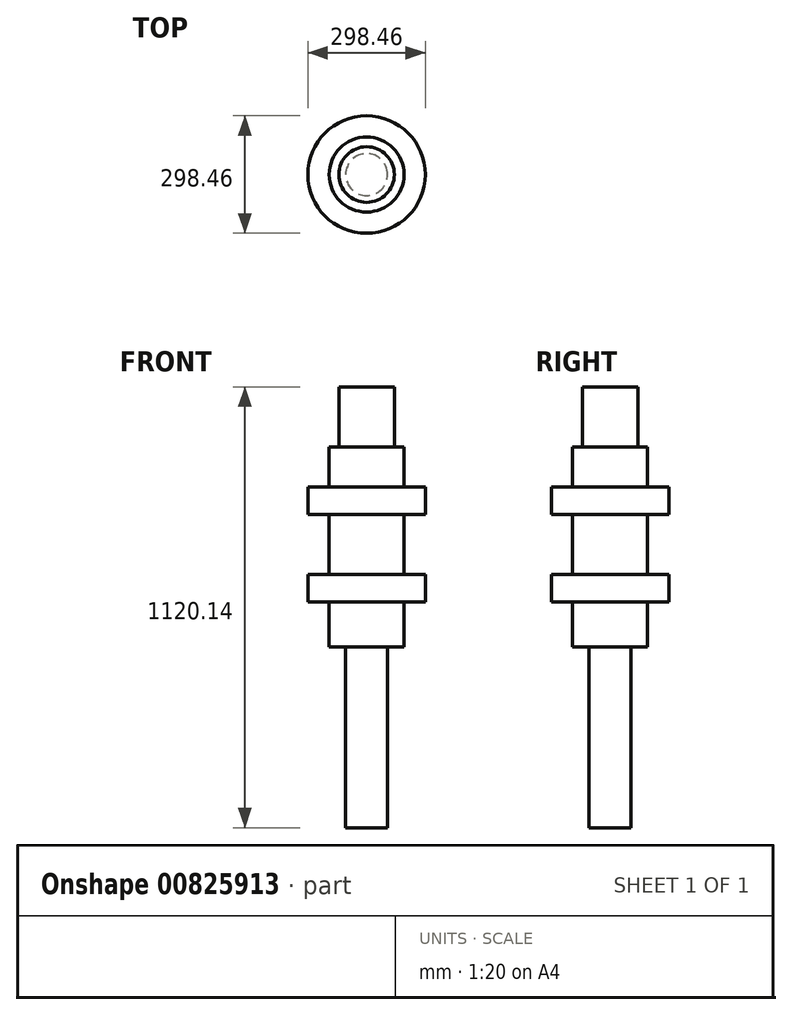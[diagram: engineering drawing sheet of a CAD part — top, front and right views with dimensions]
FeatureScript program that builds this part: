
annotation { "Feature Type Name" : "Feature", "Feature Type Description" : "" }
export const myFeature = defineFeature(function(context is Context, id is Id, definition is map)
    precondition{}
    {
        {
            var Q0;
            Q0=qCreatedBy(makeId("Right.planeOp"),FACE);
            var sketch = newSketch(context, id + "F0", { "sketchPlane" : qUnion([Q0])});
            skLineSegment(sketch, "E0", {"start": v(0, 408.3) * mm, "end": v(0, -392.94) * mm, "construction": true});
            skLineSegment(sketch, "E1", {"start": v(0, 323.85) * mm, "end": v(95.25, 323.85) * mm});
            skLineSegment(sketch, "E2", {"start": v(95.25, 323.85) * mm, "end": v(95.25, 222.25) * mm});
            skLineSegment(sketch, "E3", {"start": v(95.25, 222.25) * mm, "end": v(149.23, 222.25) * mm});
            skLineSegment(sketch, "E4", {"start": v(149.23, 222.25) * mm, "end": v(149.23, 152.4) * mm});
            skLineSegment(sketch, "E5", {"start": v(149.23, 152.4) * mm, "end": v(95.25, 152.4) * mm});
            skLineSegment(sketch, "E6", {"start": v(95.25, 152.4) * mm, "end": v(95.25, 0) * mm});
            skLineSegment(sketch, "E7", {"start": v(95.25, 0) * mm, "end": v(149.23, 0) * mm});
            skLineSegment(sketch, "E8", {"start": v(149.23, 0) * mm, "end": v(149.23, -69.85) * mm});
            skLineSegment(sketch, "E9", {"start": v(149.23, -69.85) * mm, "end": v(95.25, -69.85) * mm});
            skLineSegment(sketch, "E10", {"start": v(95.25, -69.85) * mm, "end": v(95.25, -184.15) * mm});
            skLineSegment(sketch, "E11", {"start": v(95.25, -184.15) * mm, "end": v(0, -184.15) * mm});
            skLineSegment(sketch, "E12", {"start": v(0, -184.15) * mm, "end": v(0, 323.85) * mm});
            skSolve(sketch);
        }
        {
            var Q0;
            Q0 = qSketchRegion(id + "F0", true);
            var Q1;
            Q1=sQuery(id+"F0.wireOp",EDGE,"E0");
            revolve(context, id + "F1", {"surfaceOperationType" : NewSurfaceOperationType.NEW, "entities" : qUnion([Q0]), "axis" : qUnion([Q1]), "revolveType" : RevolveType.FULL});
        }
        {
            var Q0;
            Q0=makeQuery(id+"F1.opRevolve","SWEPT_FACE",FACE,{"disambiguationData":[OSD([sQuery(id+"F0.wireOp",EDGE,"E1")])]});
            var sketch = newSketch(context, id + "F2", { "sketchPlane" : qUnion([Q0])});
            skCircle(sketch, "E13", {"center": v(0, 0) * mm, "radius": 70.63 * mm});
            skSolve(sketch);
        }
        {
            var Q0;
            Q0 = qSketchRegion(id + "F2", true);
            extrude(context, id + "F3", {"entities" : qUnion([Q0]), "operationType" : NewBodyOperationType.ADD, "depth" : 152.4 * mm, "offsetDistance" : 25.4 * mm});
        }
        {
            var Q0;
            Q0=makeQuery(id+"F1.opRevolve","SWEPT_FACE",FACE,{"disambiguationData":[OSD([sQuery(id+"F0.wireOp",EDGE,"E11")])]});
            var sketch = newSketch(context, id + "F4", { "sketchPlane" : qUnion([Q0])});
            skCircle(sketch, "E14", {"center": v(0, 0) * mm, "radius": 53.3 * mm});
            skSolve(sketch);
        }
        {
            var Q0;
            Q0 = qSketchRegion(id + "F4", true);
            extrude(context, id + "F5", {"entities" : qUnion([Q0]), "operationType" : NewBodyOperationType.ADD, "depth" : 459.74 * mm, "offsetDistance" : 25.4 * mm});
        }
    });
